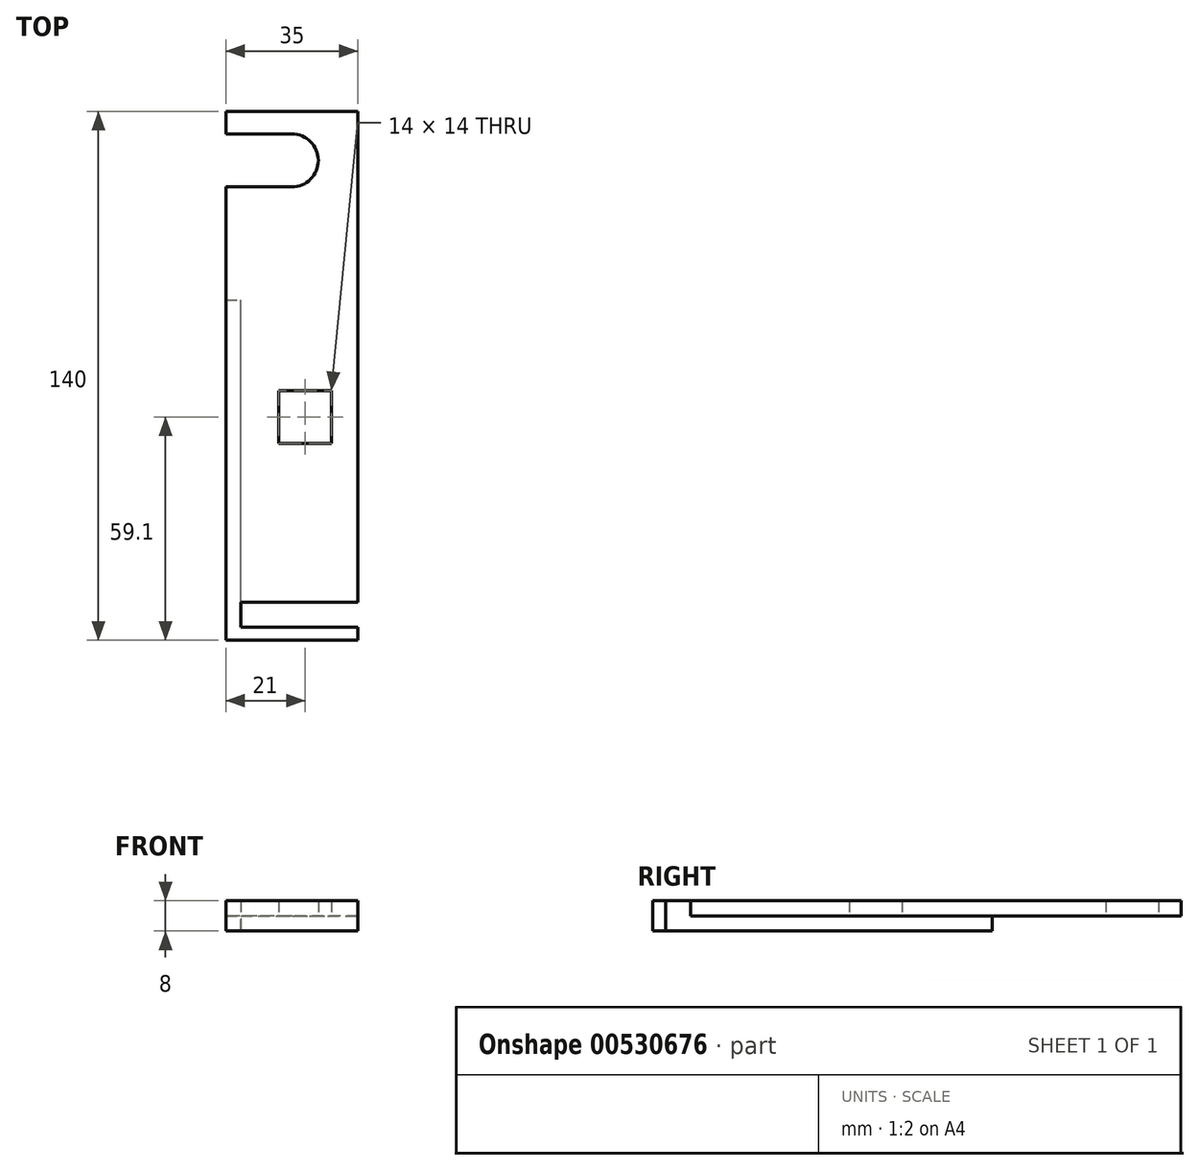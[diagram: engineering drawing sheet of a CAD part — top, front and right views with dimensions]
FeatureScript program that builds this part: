
annotation { "Feature Type Name" : "Feature", "Feature Type Description" : "" }
export const myFeature = defineFeature(function(context is Context, id is Id, definition is map)
    precondition{}
    {
        {
            var Q0;
            Q0=qCreatedBy(makeId("Top.planeOp"),FACE);
            var sketch = newSketch(context, id + "F0", { "sketchPlane" : qUnion([Q0])});
            skLineSegment(sketch, "E0.bottom", {"start": v(17.5, 70) * mm, "end": v(-17.5, 70) * mm});
            skLineSegment(sketch, "E0.top", {"start": v(17.5, -70) * mm, "end": v(-17.5, -70) * mm});
            skLineSegment(sketch, "E0.left", {"start": v(17.5, 70) * mm, "end": v(17.5, -59.9) * mm});
            skLineSegment(sketch, "E0.right", {"start": v(-17.5, 70) * mm, "end": v(-17.5, 64) * mm});
            skPoint(sketch, "E0.middle", {"position": v(0, 0) * mm});
            skLineSegment(sketch, "E1", {"start": v(17.5, -66.5) * mm, "end": v(-13.5, -66.5) * mm});
            skLineSegment(sketch, "E2", {"start": v(-13.5, -66.5) * mm, "end": v(-13.5, -59.9) * mm});
            skLineSegment(sketch, "E3", {"start": v(-13.5, -59.9) * mm, "end": v(17.5, -59.9) * mm});
            skLineSegment(sketch, "E4.trimOffspring", {"start": v(17.5, -66.5) * mm, "end": v(17.5, -70) * mm});
            skLineSegment(sketch, "E5.bottom", {"start": v(-3.5, -3.9) * mm, "end": v(10.5, -3.9) * mm});
            skLineSegment(sketch, "E5.top", {"start": v(-3.5, -17.9) * mm, "end": v(10.5, -17.9) * mm});
            skLineSegment(sketch, "E5.left", {"start": v(-3.5, -3.9) * mm, "end": v(-3.5, -17.9) * mm});
            skLineSegment(sketch, "E5.right", {"start": v(10.5, -3.9) * mm, "end": v(10.5, -17.9) * mm});
            skArc(sketch, "E6", {"start": v(0, 50) * mm, "mid": v(7, 57) * mm, "end": v(0, 64) * mm});
            skLineSegment(sketch, "E7", {"start": v(0, 50) * mm, "end": v(-17.5, 50) * mm});
            skLineSegment(sketch, "E8", {"start": v(0, 64) * mm, "end": v(-17.5, 64) * mm});
            skLineSegment(sketch, "E9.trimOffspring", {"start": v(-17.5, 50) * mm, "end": v(-17.5, -70) * mm});
            skSolve(sketch);
        }
        {
            var Q0;
            Q0 = qSketchRegion(id + "F0", true);
            extrude(context, id + "F1", {"entities" : qUnion([Q0]), "depth" : 4 * mm, "offsetDistance" : 25 * mm});
        }
        {
            var Q0;
            Q0=makeQuery(id+"F1.opExtrude","CAP_FACE",FACE,{"disambiguationData":[OSD([sQuery(id+"F0.wireOp",EDGE,"E0.bottom"),sQuery(id+"F0.wireOp",EDGE,"E0.top"),sQuery(id+"F0.wireOp",EDGE,"E0.left"),sQuery(id+"F0.wireOp",EDGE,"E0.right"),sQuery(id+"F0.wireOp",EDGE,"E1"),sQuery(id+"F0.wireOp",EDGE,"E2"),sQuery(id+"F0.wireOp",EDGE,"E3"),sQuery(id+"F0.wireOp",EDGE,"E4.trimOffspring"),sQuery(id+"F0.wireOp",EDGE,"E5.bottom"),sQuery(id+"F0.wireOp",EDGE,"E5.top"),sQuery(id+"F0.wireOp",EDGE,"E5.left"),sQuery(id+"F0.wireOp",EDGE,"E5.right"),sQuery(id+"F0.wireOp",EDGE,"E6"),sQuery(id+"F0.wireOp",EDGE,"E7"),sQuery(id+"F0.wireOp",EDGE,"E8"),sQuery(id+"F0.wireOp",EDGE,"E9.trimOffspring")])],"isStart":true});
            var sketch = newSketch(context, id + "F2", { "sketchPlane" : qUnion([Q0])});
            skLineSegment(sketch, "E10.bottom", {"start": v(-17.5, 70) * mm, "end": v(-13.5, 70) * mm});
            skLineSegment(sketch, "E10.top", {"start": v(-17.5, -20) * mm, "end": v(-13.5, -20) * mm});
            skLineSegment(sketch, "E10.left", {"start": v(-17.5, 70) * mm, "end": v(-17.5, -20) * mm});
            skLineSegment(sketch, "E10.right", {"start": v(-13.5, 70) * mm, "end": v(-13.5, -20) * mm});
            skLineSegment(sketch, "E11.bottom", {"start": v(-13.5, 70) * mm, "end": v(17.5, 70) * mm});
            skLineSegment(sketch, "E11.top", {"start": v(-13.5, 66.5) * mm, "end": v(17.5, 66.5) * mm});
            skLineSegment(sketch, "E11.left", {"start": v(-13.5, 70) * mm, "end": v(-13.5, 66.5) * mm});
            skLineSegment(sketch, "E11.right", {"start": v(17.5, 70) * mm, "end": v(17.5, 66.5) * mm});
            skSolve(sketch);
        }
        {
            var Q0;
            Q0 = qSketchRegion(id + "F2", true);
            extrude(context, id + "F3", {"entities" : qUnion([Q0]), "operationType" : NewBodyOperationType.ADD, "depth" : 4 * mm, "offsetDistance" : 25 * mm});
        }
    });
